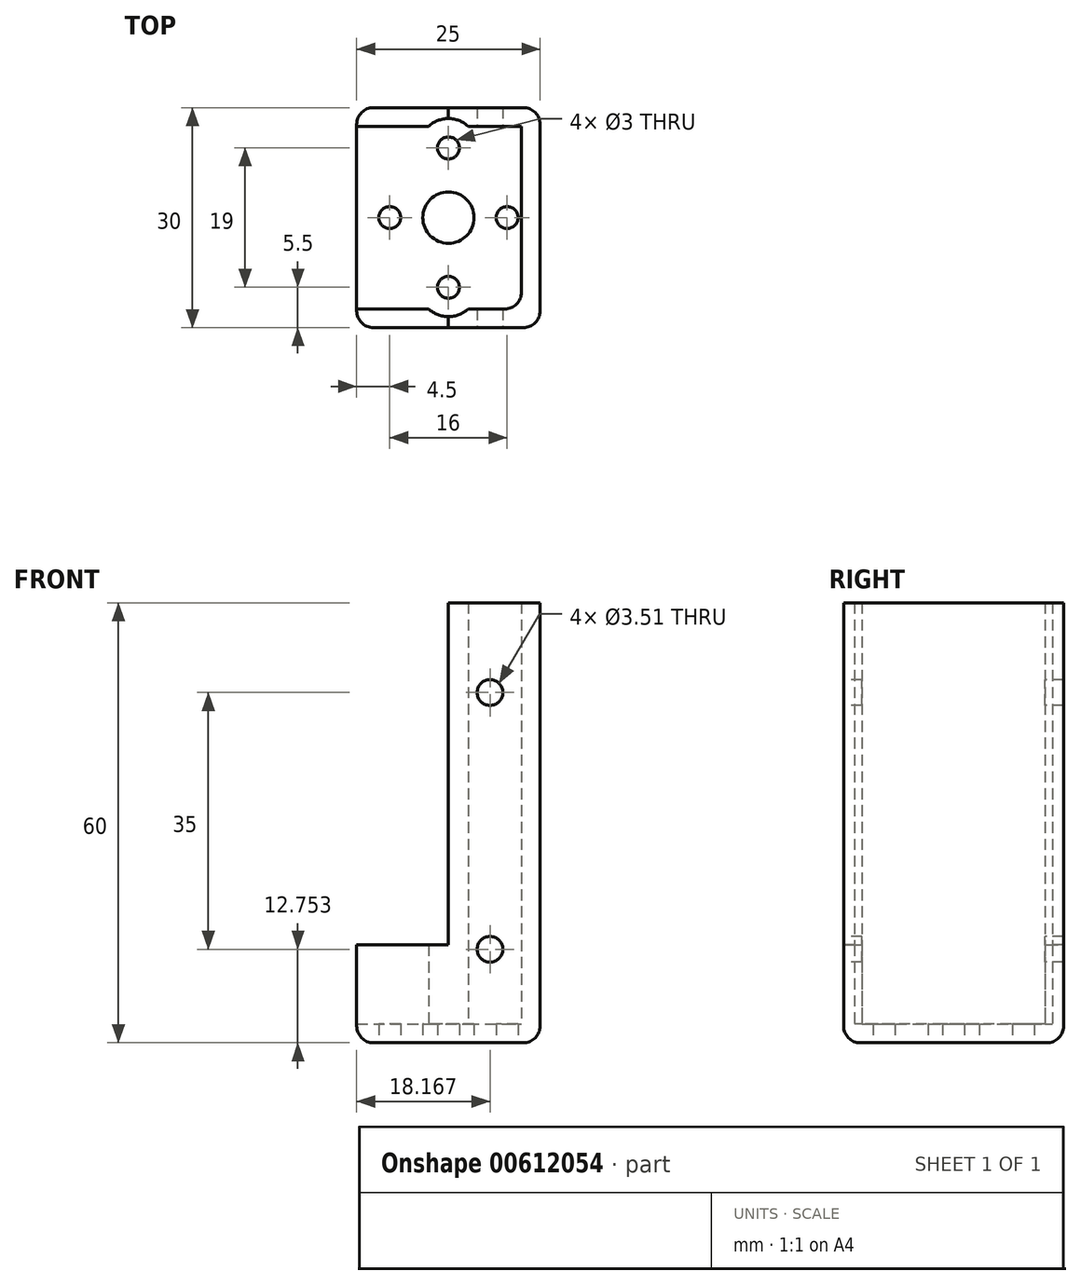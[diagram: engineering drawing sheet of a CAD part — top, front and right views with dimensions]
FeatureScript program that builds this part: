
annotation { "Feature Type Name" : "Feature", "Feature Type Description" : "" }
export const myFeature = defineFeature(function(context is Context, id is Id, definition is map)
    precondition{}
    {
        {
            var Q0;
            Q0=qCreatedBy(makeId("Top.planeOp"),FACE);
            var sketch = newSketch(context, id + "F0", { "sketchPlane" : qUnion([Q0])});
            skLineSegment(sketch, "E0.bottom", {"start": v(12.5, 15) * mm, "end": v(-12.5, 15) * mm});
            skLineSegment(sketch, "E0.top", {"start": v(12.5, -15) * mm, "end": v(-12.5, -15) * mm});
            skLineSegment(sketch, "E0.left", {"start": v(12.5, 15) * mm, "end": v(12.5, -15) * mm});
            skLineSegment(sketch, "E0.right", {"start": v(-12.5, 15) * mm, "end": v(-12.5, -15) * mm});
            skPoint(sketch, "E0.middle", {"position": v(0, 0) * mm});
            skCircle(sketch, "E1", {"center": v(0, 0) * mm, "radius": 3.5 * mm});
            skCircle(sketch, "E2", {"center": v(-8, 0) * mm, "radius": 1.5 * mm});
            skCircle(sketch, "E3", {"center": v(0, 9.5) * mm, "radius": 1.5 * mm});
            skLineSegment(sketch, "E4", {"start": v(-12.5, 0) * mm, "end": v(12.5, 0) * mm, "construction": true});
            skLineSegment(sketch, "E5", {"start": v(0, 15) * mm, "end": v(0, -15) * mm, "construction": true});
            skCircle(sketch, "E6.MirrorC", {"center": v(8, 0) * mm, "radius": 1.5 * mm});
            skCircle(sketch, "E7.MirrorC", {"center": v(0, -9.5) * mm, "radius": 1.5 * mm});
            skLineSegment(sketch, "E8.0", {"start": v(9.96, 12.46) * mm, "end": v(-9.96, 12.46) * mm});
            skLineSegment(sketch, "E8.1", {"start": v(9.96, 12.46) * mm, "end": v(9.96, -12.46) * mm});
            skLineSegment(sketch, "E8.2", {"start": v(9.96, -12.46) * mm, "end": v(-9.96, -12.46) * mm});
            skLineSegment(sketch, "E8.3", {"start": v(-9.96, 12.46) * mm, "end": v(-9.96, -12.46) * mm});
            skLineSegment(sketch, "E9", {"start": v(-9.96, -12.46) * mm, "end": v(-12.5, -12.46) * mm});
            skLineSegment(sketch, "E10", {"start": v(-9.96, 12.46) * mm, "end": v(-12.5, 12.46) * mm});
            skSolve(sketch);
        }
        {
            var Q0;
            {var subQ1=sQuery(id+"F0.wireOp",EDGE,"E0.bottom");Q0=makeQuery(id+"F0.imprint","IMPRINT",FACE,{"disambiguationData":[TD([[makeQuery(id+"F0.imprint","IMPRINT",EDGE,{"derivedFrom":subQ1}),1.0]])]});}
            var Q1;
            Q1=makeQuery(id+"F0.imprint","IMPRINT",FACE,{"disambiguationData":[TD([[makeQuery(id+"F0.imprint","IMPRINT",EDGE,{"derivedFrom":sQuery(id+"F0.wireOp",EDGE,"E1")}),-1.0]])]});
            var Q2;
            Q2=makeQuery(id+"F0.imprint","IMPRINT",FACE,{"disambiguationData":[TD([[makeQuery(id+"F0.imprint","IMPRINT",EDGE,{"derivedFrom":sQuery(id+"F0.wireOp",EDGE,"E8.3")}),-1.0]])]});
            extrude(context, id + "F1", {"entities" : qUnion([Q0, Q1, Q2]), "depth" : 2.54 * mm, "offsetDistance" : 25.4 * mm});
        }
        {
            var Q0;
            {var subQ1=sQuery(id+"F0.wireOp",EDGE,"E0.bottom");Q0=makeQuery(id+"F0.imprint","IMPRINT",FACE,{"disambiguationData":[TD([[makeQuery(id+"F0.imprint","IMPRINT",EDGE,{"derivedFrom":subQ1}),1.0]])]});}
            extrude(context, id + "F2", {"entities" : qUnion([Q0]), "operationType" : NewBodyOperationType.ADD, "depth" : 60 * mm, "offsetDistance" : 25.4 * mm});
        }
        {
            var Q0;
            {var subQ0=sQuery(id+"F0.wireOp",EDGE,"E0.top");Q0=makeQuery(id+"F2.boolean.opBoolean","MERGE",FACE,{"derivedFrom":[makeQuery(id+"F1.opExtrude","SWEPT_FACE",FACE,{"disambiguationData":[OSD([subQ0])]}),makeQuery(id+"F2.opExtrude","SWEPT_FACE",FACE,{"disambiguationData":[OSD([subQ0])]})]});}
            var sketch = newSketch(context, id + "F3", { "sketchPlane" : qUnion([Q0])});
            skCircle(sketch, "E11", {"center": v(5.67, 12.75) * mm, "radius": 1.75 * mm});
            skCircle(sketch, "E12", {"center": v(5.67, 47.75) * mm, "radius": 1.75 * mm});
            skSolve(sketch);
        }
        {
            var Q0;
            Q0 = qSketchRegion(id + "F3", true);
            extrude(context, id + "F4", {"entities" : qUnion([Q0]), "operationType" : NewBodyOperationType.REMOVE, "oppositeDirection" : true, "depth" : 34.54 * mm, "offsetDistance" : 25.4 * mm});
        }
        {
            var Q0;
            Q0=makeQuery(id+"F1.opExtrude","CAP_EDGE",EDGE,{"disambiguationData":[OSD([sQuery(id+"F0.wireOp",EDGE,"E0.left")])],"isStart":true});
            var Q1;
            Q1=makeQuery(id+"F1.opExtrude","CAP_EDGE",EDGE,{"disambiguationData":[OSD([sQuery(id+"F0.wireOp",EDGE,"E0.top")])],"isStart":true});
            var Q2;
            Q2=makeQuery(id+"F1.opExtrude","CAP_EDGE",EDGE,{"disambiguationData":[OSD([sQuery(id+"F0.wireOp",EDGE,"E0.right")])],"isStart":true});
            var Q3;
            Q3=makeQuery(id+"F1.opExtrude","CAP_EDGE",EDGE,{"disambiguationData":[OSD([sQuery(id+"F0.wireOp",EDGE,"E0.bottom")])],"isStart":true});
            var Q4;
            {var subQ0=sQuery(id+"F0.wireOp",EDGE,"E0.right");var subQ1=sQuery(id+"F0.wireOp",EDGE,"E0.top");Q4=makeQuery(id+"F2.boolean.opBoolean","MERGE",EDGE,{"derivedFrom":[makeQuery(id+"F1.opExtrude","SWEPT_EDGE",EDGE,{"disambiguationData":[OSD([subQ1,subQ0])]}),makeQuery(id+"F2.opExtrude","SWEPT_EDGE",EDGE,{"disambiguationData":[OSD([subQ1,subQ0])]})]});}
            var Q5;
            {var subQ0=sQuery(id+"F0.wireOp",EDGE,"E0.left");var subQ1=sQuery(id+"F0.wireOp",EDGE,"E0.top");Q5=makeQuery(id+"F2.boolean.opBoolean","MERGE",EDGE,{"derivedFrom":[makeQuery(id+"F1.opExtrude","SWEPT_EDGE",EDGE,{"disambiguationData":[OSD([subQ1,subQ0])]}),makeQuery(id+"F2.opExtrude","SWEPT_EDGE",EDGE,{"disambiguationData":[OSD([subQ1,subQ0])]})]});}
            var Q6;
            {var subQ0=sQuery(id+"F0.wireOp",EDGE,"E0.left");var subQ1=sQuery(id+"F0.wireOp",EDGE,"E0.bottom");Q6=makeQuery(id+"F2.boolean.opBoolean","MERGE",EDGE,{"derivedFrom":[makeQuery(id+"F1.opExtrude","SWEPT_EDGE",EDGE,{"disambiguationData":[OSD([subQ1,subQ0])]}),makeQuery(id+"F2.opExtrude","SWEPT_EDGE",EDGE,{"disambiguationData":[OSD([subQ1,subQ0])]})]});}
            var Q7;
            {var subQ0=sQuery(id+"F0.wireOp",EDGE,"E0.right");var subQ1=sQuery(id+"F0.wireOp",EDGE,"E0.bottom");Q7=makeQuery(id+"F2.boolean.opBoolean","MERGE",EDGE,{"derivedFrom":[makeQuery(id+"F1.opExtrude","SWEPT_EDGE",EDGE,{"disambiguationData":[OSD([subQ1,subQ0])]}),makeQuery(id+"F2.opExtrude","SWEPT_EDGE",EDGE,{"disambiguationData":[OSD([subQ1,subQ0])]})]});}
            var Q8;
            Q8=makeQuery(id+"F2.opExtrude","SWEPT_EDGE",EDGE,{"disambiguationData":[OSD([sQuery(id+"F0.wireOp",EDGE,"E8.1"),sQuery(id+"F0.wireOp",EDGE,"E8.2")])]});
            fillet(context, id + "F5", {"entities" : qUnion([Q0, Q1, Q2, Q3, Q4, Q5, Q6, Q7, Q8]), "radius" : 2.3 * mm, "tangentPropagation" : true, "allowEdgeOverflow" : false});
        }
        {
            var Q0;
            Q0=makeQuery(id+"F1.opExtrude","CAP_FACE",FACE,{"disambiguationData":[OSD([sQuery(id+"F0.wireOp",EDGE,"E0.bottom"),sQuery(id+"F0.wireOp",EDGE,"E0.top"),sQuery(id+"F0.wireOp",EDGE,"E0.left"),sQuery(id+"F0.wireOp",EDGE,"E0.right"),sQuery(id+"F0.wireOp",EDGE,"E1"),sQuery(id+"F0.wireOp",EDGE,"E2"),sQuery(id+"F0.wireOp",EDGE,"E3"),sQuery(id+"F0.wireOp",EDGE,"E6.MirrorC"),sQuery(id+"F0.wireOp",EDGE,"E7.MirrorC")])],"isStart":false});
            var sketch = newSketch(context, id + "F6", { "sketchPlane" : qUnion([Q0])});
            skCircle(sketch, "E13", {"center": v(0, 9.5) * mm, "radius": 4 * mm});
            skCircle(sketch, "E14", {"center": v(0, -9.5) * mm, "radius": 4 * mm});
            skSolve(sketch);
        }
        {
            var Q0;
            {var subQ0=sQuery(id+"F6.wireOp",EDGE,"E13");var subQ1=makeQuery(id+"F2.boolean.opBoolean","INTERSECT",EDGE,{"derivedFrom":[makeQuery(id+"F1.opExtrude","CAP_FACE",FACE,{"disambiguationData":[OSD([sQuery(id+"F0.wireOp",EDGE,"E0.bottom"),sQuery(id+"F0.wireOp",EDGE,"E0.top"),sQuery(id+"F0.wireOp",EDGE,"E0.left"),sQuery(id+"F0.wireOp",EDGE,"E0.right"),sQuery(id+"F0.wireOp",EDGE,"E1"),sQuery(id+"F0.wireOp",EDGE,"E2"),sQuery(id+"F0.wireOp",EDGE,"E3"),sQuery(id+"F0.wireOp",EDGE,"E6.MirrorC"),sQuery(id+"F0.wireOp",EDGE,"E7.MirrorC")])],"isStart":false}),makeQuery(id+"F2.opExtrude","SWEPT_FACE",FACE,{"disambiguationData":[OSD([sQuery(id+"F0.wireOp",EDGE,"E8.0"),sQuery(id+"F0.wireOp",EDGE,"E10")])]})]});var subQ2=makeQuery(id+"F6.imprint","INTERSECT",VERTEX,{"disambiguationData":[OD(0.0)],"derivedFrom":[subQ1,subQ0]});Q0=makeQuery(id+"F6.imprint","IMPRINT",FACE,{"disambiguationData":[TD([[makeQuery(id+"F6.imprint","IMPRINT",EDGE,{"disambiguationData":[TD([[subQ2,1.0]])],"derivedFrom":subQ0}),1.0]])]});}
            var Q1;
            {var subQ0=sQuery(id+"F6.wireOp",EDGE,"E14");var subQ1=makeQuery(id+"F2.boolean.opBoolean","INTERSECT",EDGE,{"derivedFrom":[makeQuery(id+"F1.opExtrude","CAP_FACE",FACE,{"disambiguationData":[OSD([sQuery(id+"F0.wireOp",EDGE,"E0.bottom"),sQuery(id+"F0.wireOp",EDGE,"E0.top"),sQuery(id+"F0.wireOp",EDGE,"E0.left"),sQuery(id+"F0.wireOp",EDGE,"E0.right"),sQuery(id+"F0.wireOp",EDGE,"E1"),sQuery(id+"F0.wireOp",EDGE,"E2"),sQuery(id+"F0.wireOp",EDGE,"E3"),sQuery(id+"F0.wireOp",EDGE,"E6.MirrorC"),sQuery(id+"F0.wireOp",EDGE,"E7.MirrorC")])],"isStart":false}),makeQuery(id+"F2.opExtrude","SWEPT_FACE",FACE,{"disambiguationData":[OSD([sQuery(id+"F0.wireOp",EDGE,"E8.2"),sQuery(id+"F0.wireOp",EDGE,"E9")])]})]});var subQ2=makeQuery(id+"F6.imprint","INTERSECT",VERTEX,{"disambiguationData":[OD(0.0)],"derivedFrom":[subQ1,subQ0]});Q1=makeQuery(id+"F6.imprint","IMPRINT",FACE,{"disambiguationData":[TD([[makeQuery(id+"F6.imprint","IMPRINT",EDGE,{"disambiguationData":[TD([[subQ2,-1.0]])],"derivedFrom":subQ0}),1.0]])]});}
            extrude(context, id + "F7", {"entities" : qUnion([Q0, Q1]), "operationType" : NewBodyOperationType.REMOVE, "depth" : 61.82 * mm, "offsetDistance" : 25.4 * mm});
        }
        {
            var Q0;
            {var subQ0=sQuery(id+"F0.wireOp",EDGE,"E0.top");Q0=makeQuery(id+"F2.boolean.opBoolean","MERGE",FACE,{"derivedFrom":[makeQuery(id+"F1.opExtrude","SWEPT_FACE",FACE,{"disambiguationData":[OSD([subQ0])]}),makeQuery(id+"F2.opExtrude","SWEPT_FACE",FACE,{"disambiguationData":[OSD([subQ0])]})]});}
            var sketch = newSketch(context, id + "F8", { "sketchPlane" : qUnion([Q0])});
            skLineSegment(sketch, "E15.bottom", {"start": v(-17.17, 64.06) * mm, "end": v(0, 64.06) * mm});
            skLineSegment(sketch, "E15.top", {"start": v(-17.17, 13.36) * mm, "end": v(0, 13.36) * mm});
            skLineSegment(sketch, "E15.left", {"start": v(-17.17, 64.06) * mm, "end": v(-17.17, 13.36) * mm});
            skLineSegment(sketch, "E15.right", {"start": v(0, 64.06) * mm, "end": v(0, 13.36) * mm});
            skSolve(sketch);
        }
        {
            var Q0;
            {var subQ1=sQuery(id+"F8.wireOp",EDGE,"E15.bottom");Q0=makeQuery(id+"F8.imprint","IMPRINT",FACE,{"disambiguationData":[TD([[makeQuery(id+"F8.imprint","IMPRINT",EDGE,{"derivedFrom":subQ1}),-1.0]])]});}
            var Q1;
            {var subQ0=sQuery(id+"F8.wireOp",EDGE,"E15.right");var subQ1=sQuery(id+"F8.wireOp",EDGE,"E15.top");var subQ2=makeQuery(id+"F8.imprint","INTERSECT",VERTEX,{"derivedFrom":[subQ1,subQ0]});Q1=makeQuery(id+"F8.imprint","IMPRINT",FACE,{"disambiguationData":[TD([[makeQuery(id+"F8.imprint","IMPRINT",EDGE,{"disambiguationData":[TD([[subQ2,1.0]])],"derivedFrom":subQ0}),-1.0]])]});}
            extrude(context, id + "F9", {"entities" : qUnion([Q0, Q1]), "operationType" : NewBodyOperationType.REMOVE, "oppositeDirection" : true, "depth" : 44.96 * mm, "offsetDistance" : 25.4 * mm});
        }
    });
